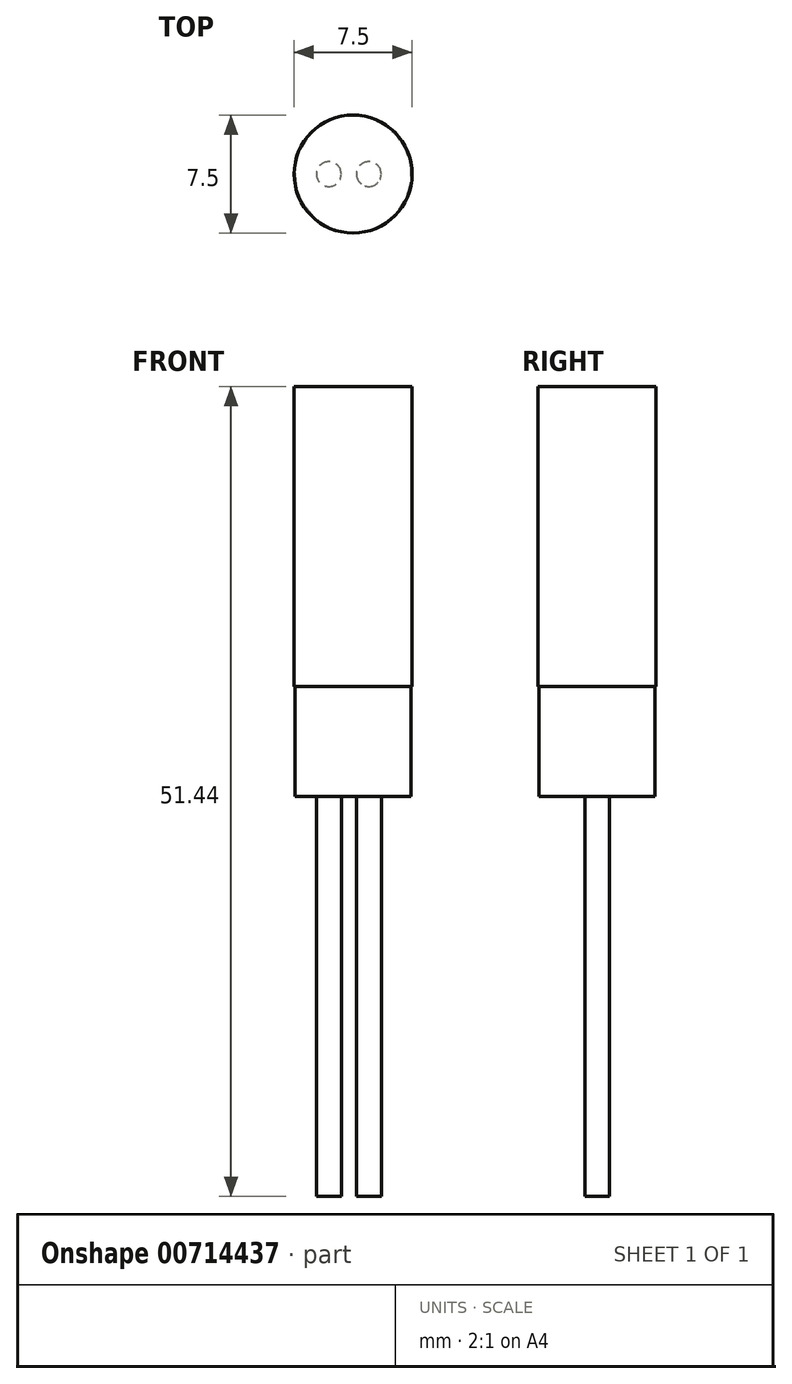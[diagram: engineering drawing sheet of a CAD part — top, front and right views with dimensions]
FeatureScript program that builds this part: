
annotation { "Feature Type Name" : "Feature", "Feature Type Description" : "" }
export const myFeature = defineFeature(function(context is Context, id is Id, definition is map)
    precondition{}
    {
        {
            var Q0;
            Q0=qCreatedBy(makeId("Top.planeOp"),FACE);
            var sketch = newSketch(context, id + "F0", { "sketchPlane" : qUnion([Q0])});
            skCircle(sketch, "E0", {"center": v(0, 0) * mm, "radius": 3.68 * mm});
            skSolve(sketch);
        }
        {
            var Q0;
            Q0=qSketchRegion(id+"F0",true);
            extrude(context, id + "F1", {"entities" : qUnion([Q0]), "oppositeDirection" : true, "depth" : 7 * mm});
        }
        {
            var Q0;
            Q0=makeQuery(id+"F1.opExtrude","CAP_FACE",FACE,{"disambiguationData":[OSD([sQuery(id+"F0.wireOp",EDGE,"E0")])],"isStart":false});
            var sketch = newSketch(context, id + "F2", { "sketchPlane" : qUnion([Q0])});
            skLineSegment(sketch, "E1", {"start": v(-1.54, 0) * mm, "end": v(1, 0) * mm});
            skCircle(sketch, "E2", {"center": v(-1.54, 0) * mm, "radius": 0.79 * mm});
            skCircle(sketch, "E3", {"center": v(1, 0) * mm, "radius": 0.79 * mm});
            skSolve(sketch);
        }
        {
            var Q0;
            Q0=qSketchRegion(id+"F2",true);
            extrude(context, id + "F3", {"entities" : qUnion([Q0]), "operationType" : NewBodyOperationType.ADD, "depth" : 25.4 * mm});
        }
        {
            var Q0;
            Q0=makeQuery(id+"F1.opExtrude","CAP_FACE",FACE,{"disambiguationData":[OSD([sQuery(id+"F0.wireOp",EDGE,"E0")])],"isStart":true});
            var sketch = newSketch(context, id + "F4", { "sketchPlane" : qUnion([Q0])});
            skCircle(sketch, "E4", {"center": v(0, 0) * mm, "radius": 3.75 * mm});
            skSolve(sketch);
        }
        {
            var Q0;
            Q0=qSketchRegion(id+"F4",true);
            extrude(context, id + "F5", {"entities" : qUnion([Q0]), "operationType" : NewBodyOperationType.ADD, "depth" : 19.05 * mm});
        }
    });
